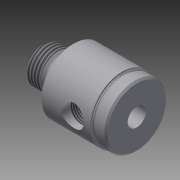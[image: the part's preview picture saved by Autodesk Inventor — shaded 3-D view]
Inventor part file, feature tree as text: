
AUTODESK INVENTOR PART (.ipt)
format: ipt  version: 2014 SP2 (Build 180246200, 246)  size: 260,096 bytes
history: native  units: in
note: dims shown in document units (in); Inventor stores cm internally (conversion verified against a paired STEP export)
features: other x119, sketch x5, revolve x4, thread x2, hole x1
ambient origin geometry x8: Origin, YZ Plane, XZ Plane, XY Plane, X Axis, Y Axis, Z Axis, Center Point
bodies: Solid1 (feature_tree)
feature tree (131):
  revolve  "Revolution1"  [1 undecoded]
  thread  "Thread1"  [1 undecoded]
  revolve  "Revolution2"  Angle=360.0deg
  hole  "Hole1"  [1 undecoded]
  revolve  "Revolution3"  [1 undecoded]
  thread  "Thread2"  [1 undecoded]
  revolve  "Revolution4"  [1 undecoded]
  other  "dp1_XY"
  other  "dp1_YZ"
  other  "dp1_ZX"
  other  "dp1_X"
  other  "dp1_Y"
  other  "dp1_Z"
  other  "dp1_Center"
  other  "dp2_XY"
  other  "dp2_YZ"
  other  "dp2_ZX"
  other  "dp2_X"
  other  "dp2_Y"
  other  "dp2_Z"
  other  "dp2_Center"
  other  "hh_XY"
  other  "hh_YZ"
  other  "hh_ZX"
  other  "hh_X"
  other  "hh_Y"
  other  "hh_Z"
  other  "hh_Center"
  other  "port_XY"
  other  "port_YZ"
  other  "port_ZX"
  other  "port_X"
  other  "port_Y"
  other  "port_Z"
  other  "port_Center"
  other  "rod_guide_XY"
  other  "rod_guide_YZ"
  other  "rod_guide_ZX"
  other  "rod_guide_X"
  other  "rod_guide_Y"
  other  "rod_guide_Z"
  other  "rod_guide_Center"
  other  "s1_XY"
  other  "s1_YZ"
  other  "s1_ZX"
  other  "s1_X"
  other  "s1_Y"
  other  "s1_Z"
  other  "s1_Center"
  other  "s2_XY"
  other  "s2_YZ"
  other  "s2_ZX"
  other  "s2_X"
  other  "s2_Y"
  other  "s2_Z"
  other  "s2_Center"
  other  "t1_XY"
  other  "t1_YZ"
  other  "t1_ZX"
  other  "t1_X"
  other  "t1_Y"
  other  "t1_Z"
  other  "t1_Center"
  other  "t111_XY"
  other  "t111_YZ"
  other  "t111_ZX"
  other  "t111_X"
  other  "t111_Y"
  other  "t111_Z"
  other  "t111_Center"
  other  "to_foot_bracket_XY"
  other  "to_foot_bracket_YZ"
  other  "to_foot_bracket_ZX"
  other  "to_foot_bracket_X"
  other  "to_foot_bracket_Y"
  other  "to_foot_bracket_Z"
  other  "to_foot_bracket_Center"
  other  "to_nut_XY"
  other  "to_nut_YZ"
  other  "to_nut_ZX"
  other  "to_nut_X"
  other  "to_nut_Y"
  other  "to_nut_Z"
  other  "to_nut_Center"
  other  "to_rod_XY"
  other  "to_rod_YZ"
  other  "to_rod_ZX"
  other  "to_rod_X"
  other  "to_rod_Y"
  other  "to_rod_Z"
  other  "to_rod_Center"
  other  "to_screw_XY"
  other  "to_screw_YZ"
  other  "to_screw_ZX"
  other  "to_screw_X"
  other  "to_screw_Y"
  other  "to_screw_Z"
  other  "to_screw_Center"
  other  "to_trunnion_brackets_XY"
  other  "to_trunnion_brackets_YZ"
  other  "to_trunnion_brackets_ZX"
  other  "to_trunnion_brackets_X"
  other  "to_trunnion_brackets_Y"
  other  "to_trunnion_brackets_Z"
  other  "to_trunnion_brackets_Center"
  other  "to_trunnion_brackets1_XY"
  other  "to_trunnion_brackets1_YZ"
  other  "to_trunnion_brackets1_ZX"
  other  "to_trunnion_brackets1_X"
  other  "to_trunnion_brackets1_Y"
  other  "to_trunnion_brackets1_Z"
  other  "to_trunnion_brackets1_Center"
  other  "to_trunnion_brackets2_XY"
  other  "to_trunnion_brackets2_YZ"
  other  "to_trunnion_brackets2_ZX"
  other  "to_trunnion_brackets2_X"
  other  "to_trunnion_brackets2_Y"
  other  "to_trunnion_brackets2_Z"
  other  "to_trunnion_brackets2_Center"
  other  "to_tube_XY"
  other  "to_tube_YZ"
  other  "to_tube_ZX"
  other  "to_tube_X"
  other  "to_tube_Y"
  other  "to_tube_Z"
  other  "to_tube_Center"
  sketch  "Sketch_2"  dims[d0=360.0deg d1=0.2297in d2=0.0in d3=360.0deg]
  sketch  "Sketch_3"  dims[d4=0.316in d5=0.75in d6=0.376in d7=0.25in d8=90.0deg d9=1.625in d10=0.0in d11=360.0deg]
  sketch  "Sketch3"  dims[d12=0.2251in d13=0.0in d14=360.0deg]
  sketch  "Sketch_40"  dims[d15=0.0in d16=0.0in d17=0.0in d18=0.0in d19=0.0in d20=0.0in]
  sketch  "Sketch_47"
note: 6 required parameter values undecoded (feature->parameter linkage not recoverable at this tier; creation-order binding heuristic only, values carry confidence <= 0.55)